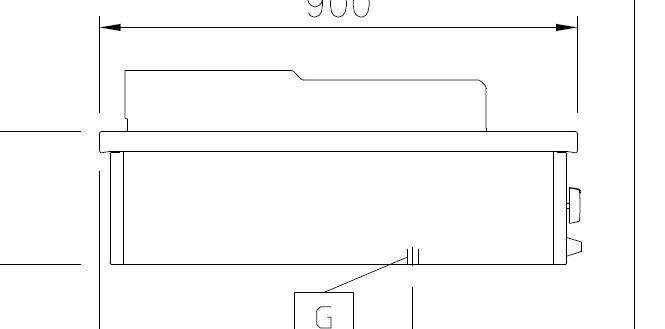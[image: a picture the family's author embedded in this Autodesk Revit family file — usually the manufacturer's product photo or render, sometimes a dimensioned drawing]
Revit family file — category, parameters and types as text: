
# Revit family: QF_ELECTROLUXPROFESSIONAL_593301_MCDAABDOVO
name_source: partatom
category: Specialty Equipment
revit_build: Autodesk Revit 2018 (Build: 20190510_1515(x64)
units: mm (PartAtom-declared; Revit-internal decimal feet)

## family parameters
Always vertical = Yes
Cut with Voids When Loaded = No
Part Type = Normal
Room Calculation Point = No
Round Connector Dimension = Use Diameter
Shared = No
Work Plane-Based = No

## types (1)
- Standard
    Accessory = Yes
    Cold Water Size = 0"
    Compressed Air Pressure = 0.00 psi
    Compressed Air Size = 0"
    Compressed Air Volume = 0 GPM
    Condensate Return Size = 0"
    Cycle = 0 Hz
    Depth Actual = 900 mm  [stored 2.95276 ft]
    Description = GAS CHARGRILL,TOWNGAS,1S,BS,400X900X250H
    Direct Waste Size = 0"
    Gas Input Pressure = 0.8
    Gas KW = 9.5
    Gas Size = 1"
    HP = 0 HP
    Height Actual = 250 mm  [stored 0.82021 ft]
    Hot Water Size = 0"
    Item Number = 593301
    Length Actual = 400 mm  [stored 1.31234 ft]
    Manufacturer = Electrolux Professional
    Model = MCDAABDOVO
    Phase = 0
    Refrigerant Compressor Remote = Yes
    Refrigeration Liquid Line Size = 0 mm  [stored 0 ft]
    Refrigeration Suction Line Size = 0 mm  [stored 0 ft]
    Steam Pounds per Hour = 0
    Steam Supply Maximum Pressure = 0.00 psi
    Steam Supply Minimum Pressure = 0.00 psi
    Steam Supply Size = 0"
    URL = http://professional.electrolux.com
    URL Manufacturer = http://professional.electrolux.com
    Volts = 0 V
    Watts = 0 W
    Weight = 65.00 kg

note: source unit labels omitted for Gas Input Pressure — the stored unit's dimension contradicts the parameter name (converter mislabeling)

note: [stored X ft] marks values corroborated as IEEE doubles in the binary element streams (Revit-internal decimal feet)

## geometry (parser evidence)
native form markers: Blend x20, Sweep x15
no freeform markers — native parametric forms only
